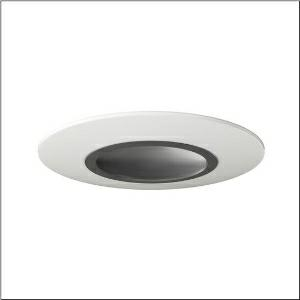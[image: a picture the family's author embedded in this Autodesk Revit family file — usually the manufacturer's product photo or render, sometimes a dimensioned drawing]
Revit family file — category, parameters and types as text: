
# Revit family: rondel_21_0md5307l1830
name_source: partatom
category: Lighting Fixtures
units: mm (PartAtom-declared; Revit-internal decimal feet)

## family parameters
Cut with Voids When Loaded = No
Host = Face
Light Source = No
Part Type = Normal
Room Calculation Point = No
Round Connector Dimension = Use Diameter
Shared = No

## types (1)
- Rondel 21 (1 x LED 3000K / CRI = 80 (unbekannt), 1800 lm, 3000K)
    Apparent Load = 18 VA
    CIE Flux Codes = 43 74 92 91 100
    Color Rendering = 80
    Color Temperature = 3000K
    Default Elevation = 1800 mm  [stored 5.90551 ft]
    Description = Rondel 21, wall and ceiling luminaire, of PC, opal, light emission: direct distribution, installation type: surface-mounted, LED rated luminous flux: 1.800 lm, light colour: 830, colour temperature: 3000K, control gear: ECG, with terminal, 2-pole, mains connection: 220..240V, AC, 50/60Hz, rated input power: 18W, housing, round, of sheet steel, powder-coated, white, diameter: 380 mm, height: 28mm, cover, of PC, graphite (RAL 7037), protection rating (complete): IP40, insulation class (complete): insulation class II (safety insulation), certification: CE, impact resistance: IK03, permissible ambient temperature for indoor applications: -20..+40°C, permissible storage temperature: -20..+80°C, packaging unit: 1 piece
    Height = 28 mm
    Lamp = 1 x LED 3000K / CRI >= 80 (unbekannt)
    Lamp Light Flux = 1800 lm
    Lamp count = 1
    Length = 380 mm
    Luminous efficacy = 100 lm/W
    Manufacturer = Siteco
    ModVariant = No
    Model = 0MD5307L1830
    Mounting Place = Ceiling
    Mounting Type = Surface mounted
    Number of Poles = 1
    OnlyDefault = Yes
    Power Factor = 1
    Product Name = Rondel 21
    Product group = wall and ceiling luminaire
    ProductGroupID = 301
    Protection Class = Protection class II
    Protection Degree = IP 40
    RLX_Detail_Level = 1
    RlxData = <blob elided: 61645 chars, md5=dd38baf5>
    Socket = socket
    Standby Power = 0 W
    System Light Flux = 1800 lm
    System Power = 18 W
    Type Comments = Product without accessories
    Type Image = l_1005688.jpg
    URL = http://relux.com
    VarID = ---
    Voltage = 0 V
    Weight = 0.00 kg
    Width = 0 mm  [stored 0 ft]

note: [stored X ft] marks values corroborated as IEEE doubles in the binary element streams (Revit-internal decimal feet)

## geometry (parser evidence)
native form markers: Blend x4, Sweep x13
no freeform markers — native parametric forms only
